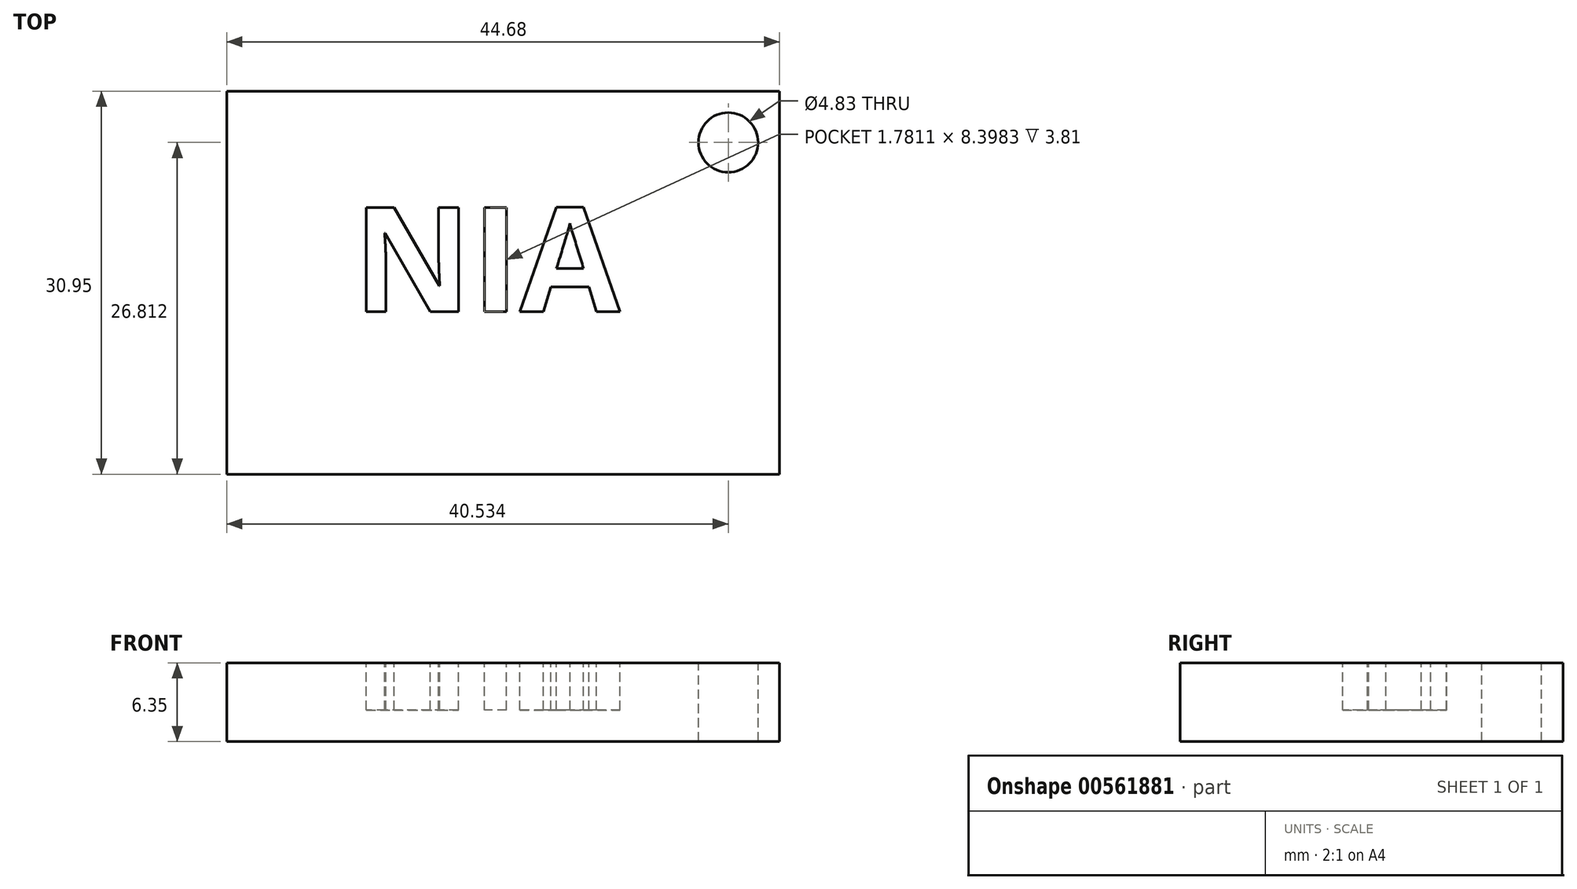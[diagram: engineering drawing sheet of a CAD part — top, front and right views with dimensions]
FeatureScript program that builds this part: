
annotation { "Feature Type Name" : "Feature", "Feature Type Description" : "" }
export const myFeature = defineFeature(function(context is Context, id is Id, definition is map)
    precondition{}
    {
        {
            var Q0;
            Q0=qCreatedBy(makeId("Top.planeOp"),FACE);
            var sketch = newSketch(context, id + "F0", { "sketchPlane" : qUnion([Q0])});
            skLineSegment(sketch, "E0.bottom", {"start": v(0, 0) * mm, "end": v(-44.68, 0) * mm});
            skLineSegment(sketch, "E0.top", {"start": v(0, 30.95) * mm, "end": v(-44.68, 30.95) * mm});
            skLineSegment(sketch, "E0.left", {"start": v(0, 0) * mm, "end": v(0, 30.95) * mm});
            skLineSegment(sketch, "E0.right", {"start": v(-44.68, 0) * mm, "end": v(-44.68, 30.95) * mm});
            skSolve(sketch);
        }
        {
            var Q0;
            Q0=makeQuery(id+"F0.imprint","IMPRINT",FACE,{"disambiguationData":[TD([[makeQuery(id+"F0.imprint","IMPRINT",EDGE,{"derivedFrom":sQuery(id+"F0.wireOp",EDGE,"E0.bottom")}),-1.0]])]});
            extrude(context, id + "F1", {"entities" : qUnion([Q0]), "depth" : 6.35 * mm, "offsetDistance" : 25.4 * mm});
        }
        {
            var Q0;
            Q0=makeQuery(id+"F1.opExtrude","CAP_FACE",FACE,{"disambiguationData":[OSD([sQuery(id+"F0.wireOp",EDGE,"E0.bottom"),sQuery(id+"F0.wireOp",EDGE,"E0.top"),sQuery(id+"F0.wireOp",EDGE,"E0.left"),sQuery(id+"F0.wireOp",EDGE,"E0.right")])],"isStart":false});
            var sketch = newSketch(context, id + "F2", { "sketchPlane" : qUnion([Q0])});
            skText(sketch, "E1", { "text": "NIA", "fontName": "OpenSans-Bold.ttf"});
            const initialGuessF2  = {"E1": [-0.03446, 0.01314, 1, 0, 0.00847]};
            skSetInitialGuess(sketch, initialGuessF2);
            skSolve(sketch);
        }
        {
            var Q0;
            Q0=makeQuery(id+"F2.imprint","IMPRINT",FACE,{"disambiguationData":[TD([[makeQuery(id+"F2.imprint","IMPRINT",EDGE,{"derivedFrom":sQuery(id+"F2.wireOp",EDGE,"E1.sketch_text.stroke-0")}),1.0]])]});
            var sketch = newSketch(context, id + "F3", { "sketchPlane" : qUnion([Q0])});
            skCircle(sketch, "E2", {"center": v(-4.15, 26.81) * mm, "radius": 2.41 * mm});
            skSolve(sketch);
        }
        {
            var Q0;
            Q0=sQuery(id+"F3.wireOp",VERTEX,"E2.center");
            var Q1;
            Q1=makeQuery(id+"F1.opExtrude","SWEPT_BODY",BODY,{"disambiguationData":[OSD([sQuery(id+"F0.wireOp",EDGE,"E0.bottom"),sQuery(id+"F0.wireOp",EDGE,"E0.top"),sQuery(id+"F0.wireOp",EDGE,"E0.left"),sQuery(id+"F0.wireOp",EDGE,"E0.right")])]});
            hole(context, id + "F4", {"style" : HoleStyle.SIMPLE, "endStyle" : HoleEndStyle.THROUGH, "holeDiameter" : 4.83 * mm, "isTappedThrough" : true, "tappedDepth" : 12.7 * mm, "tapClearance" : 3, "locations" : qUnion([Q0]), "scope" : qUnion([Q1])});
        }
        {
            var Q0;
            Q0 = qSketchRegion(id + "F2", true);
            extrude(context, id + "F5", {"entities" : qUnion([Q0]), "operationType" : NewBodyOperationType.REMOVE, "oppositeDirection" : true, "depth" : 3.8 * mm, "offsetDistance" : 25.4 * mm});
        }
    });
